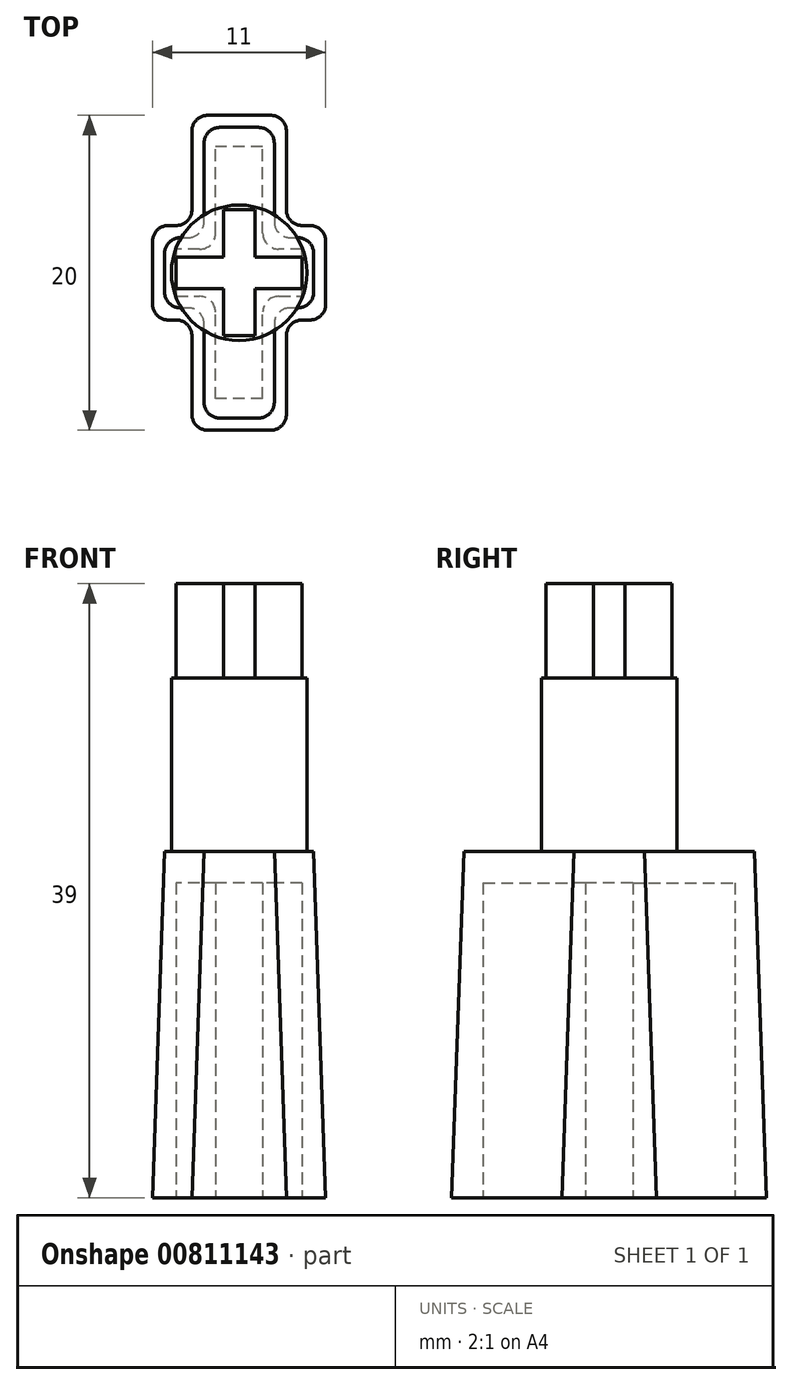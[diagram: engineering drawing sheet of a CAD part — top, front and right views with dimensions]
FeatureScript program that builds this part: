
annotation { "Feature Type Name" : "Feature", "Feature Type Description" : "" }
export const myFeature = defineFeature(function(context is Context, id is Id, definition is map)
    precondition{}
    {
        {
            var Q0;
            Q0=qCreatedBy(makeId("Top.planeOp"),FACE);
            var sketch = newSketch(context, id + "F0", { "sketchPlane" : qUnion([Q0])});
            skLineSegment(sketch, "E0.bottom", {"start": v(1.5, -8) * mm, "end": v(-1.5, -8) * mm});
            skLineSegment(sketch, "E0.top", {"start": v(1.5, 8) * mm, "end": v(-1.5, 8) * mm});
            skLineSegment(sketch, "E0.left", {"start": v(1.5, -8) * mm, "end": v(1.5, 8) * mm});
            skLineSegment(sketch, "E0.right", {"start": v(-1.5, -8) * mm, "end": v(-1.5, 8) * mm});
            skPoint(sketch, "E0.middle", {"position": v(0, 0) * mm});
            skLineSegment(sketch, "E1", {"start": v(-1.5, 1.5) * mm, "end": v(-4, 1.5) * mm});
            skLineSegment(sketch, "E2", {"start": v(-4, 1.5) * mm, "end": v(-4, -1.5) * mm});
            skLineSegment(sketch, "E3", {"start": v(-4, -1.5) * mm, "end": v(-1.5, -1.5) * mm});
            skLineSegment(sketch, "E4", {"start": v(1.5, 1.5) * mm, "end": v(1.5, -1.5) * mm});
            skLineSegment(sketch, "E5", {"start": v(1.5, -1.5) * mm, "end": v(4, -1.5) * mm});
            skLineSegment(sketch, "E6", {"start": v(4, -1.5) * mm, "end": v(4, 1.5) * mm});
            skLineSegment(sketch, "E7", {"start": v(4, 1.5) * mm, "end": v(1.5, 1.5) * mm});
            skPoint(sketch, "E8", {"position": v(-4, 0) * mm});
            skPoint(sketch, "E9", {"position": v(4, 0) * mm});
            skSolve(sketch);
        }
        {
            var Q0;
            Q0=qCreatedBy(makeId("Top.planeOp"),FACE);
            var sketch = newSketch(context, id + "F1", { "sketchPlane" : qUnion([Q0])});
            skLineSegment(sketch, "E10.bottom", {"start": v(3, 10) * mm, "end": v(-3, 10) * mm});
            skLineSegment(sketch, "E10.top", {"start": v(3, -10) * mm, "end": v(-3, -10) * mm});
            skLineSegment(sketch, "E10.left", {"start": v(3, 10) * mm, "end": v(3, -10) * mm});
            skLineSegment(sketch, "E10.right", {"start": v(-3, 10) * mm, "end": v(-3, -10) * mm});
            skPoint(sketch, "E10.middle", {"position": v(0, 0) * mm});
            skPoint(sketch, "E11", {"position": v(-3, -3) * mm});
            skPoint(sketch, "E12", {"position": v(-3, 3) * mm});
            skPoint(sketch, "E13", {"position": v(3, 3) * mm});
            skPoint(sketch, "E14", {"position": v(3, -3) * mm});
            skLineSegment(sketch, "E15", {"start": v(-3, 3) * mm, "end": v(-5.5, 3) * mm});
            skLineSegment(sketch, "E16", {"start": v(-5.5, 3) * mm, "end": v(-5.5, -3) * mm});
            skLineSegment(sketch, "E17", {"start": v(-5.5, -3) * mm, "end": v(-3, -3) * mm});
            skLineSegment(sketch, "E18", {"start": v(3, 3) * mm, "end": v(5.5, 3) * mm});
            skLineSegment(sketch, "E19", {"start": v(5.5, 3) * mm, "end": v(5.5, -3) * mm});
            skLineSegment(sketch, "E20", {"start": v(5.5, -3) * mm, "end": v(3, -3) * mm});
            skPoint(sketch, "E21", {"position": v(-5.5, 0) * mm});
            skPoint(sketch, "E22", {"position": v(5.5, 0) * mm});
            skSolve(sketch);
        }
        {
            var Q0;
            Q0=makeQuery(id+"F1.imprint","IMPRINT",FACE,{"disambiguationData":[TD([[makeQuery(id+"F1.imprint","IMPRINT",EDGE,{"derivedFrom":sQuery(id+"F1.wireOp",EDGE,"E10.bottom")}),1.0]])]});
            var Q1;
            {var subQ0=sQuery(id+"F1.wireOp",EDGE,"E15");Q1=makeQuery(id+"F1.imprint","IMPRINT",FACE,{"disambiguationData":[TD([[makeQuery(id+"F1.imprint","IMPRINT",EDGE,{"derivedFrom":subQ0}),1.0]])]});}
            var Q2;
            {var subQ0=sQuery(id+"F1.wireOp",EDGE,"E18");Q2=makeQuery(id+"F1.imprint","IMPRINT",FACE,{"disambiguationData":[TD([[makeQuery(id+"F1.imprint","IMPRINT",EDGE,{"derivedFrom":subQ0}),-1.0]])]});}
            extrude(context, id + "F2", {"entities" : qUnion([Q0, Q1, Q2]), "depth" : 22 * mm, "offsetDistance" : 25 * mm, "hasDraft" : true, "draftAngle" : 2 * degree, "draftPullDirection" : true});
        }
        {
            var Q0;
            Q0 = qSketchRegion(id + "F0", true);
            extrude(context, id + "F3", {"entities" : qUnion([Q0]), "operationType" : NewBodyOperationType.REMOVE, "depth" : 20 * mm, "offsetDistance" : 25 * mm});
        }
        {
            var Q0;
            Q0=makeQuery(id+"F2.opExtrude","CAP_FACE",FACE,{"disambiguationData":[OSD([sQuery(id+"F1.wireOp",EDGE,"E10.bottom"),sQuery(id+"F1.wireOp",EDGE,"E10.top"),sQuery(id+"F1.wireOp",EDGE,"E10.left"),sQuery(id+"F1.wireOp",EDGE,"E10.right")])],"isStart":false});
            cPlane(context, id + "F4", {"entities" : qUnion([Q0]), "cplaneType" : CPlaneType.OFFSET, "offset" : 11 * mm, "width" : 150 * mm, "height" : 150 * mm});
        }
        {
            var Q0;
            Q0=qCreatedBy(id+"F4.planeOp",FACE);
            var sketch = newSketch(context, id + "F5", { "sketchPlane" : qUnion([Q0])});
            skLineSegment(sketch, "E23.bottom", {"start": v(4.5, -3) * mm, "end": v(-4.5, -3) * mm});
            skLineSegment(sketch, "E23.top", {"start": v(4.5, 3) * mm, "end": v(-4.5, 3) * mm});
            skLineSegment(sketch, "E23.left", {"start": v(4.5, -3) * mm, "end": v(4.5, 3) * mm});
            skLineSegment(sketch, "E23.right", {"start": v(-4.5, -3) * mm, "end": v(-4.5, 3) * mm});
            skPoint(sketch, "E23.middle", {"position": v(0, 0) * mm});
            skLineSegment(sketch, "E24.bottom", {"start": v(3, 5.5) * mm, "end": v(-3, 5.5) * mm});
            skLineSegment(sketch, "E24.top", {"start": v(3, -5.5) * mm, "end": v(-3, -5.5) * mm});
            skLineSegment(sketch, "E24.left", {"start": v(3, 5.5) * mm, "end": v(3, -5.5) * mm});
            skLineSegment(sketch, "E24.right", {"start": v(-3, 5.5) * mm, "end": v(-3, -5.5) * mm});
            skLineSegment(sketch, "E25.bottom", {"start": v(4, -1) * mm, "end": v(-4, -1) * mm});
            skLineSegment(sketch, "E25.top", {"start": v(4, 1) * mm, "end": v(-4, 1) * mm});
            skLineSegment(sketch, "E25.left", {"start": v(4, -1) * mm, "end": v(4, 1) * mm});
            skLineSegment(sketch, "E25.right", {"start": v(-4, -1) * mm, "end": v(-4, 1) * mm});
            skLineSegment(sketch, "E26.bottom", {"start": v(-1, 4) * mm, "end": v(1, 4) * mm});
            skLineSegment(sketch, "E26.top", {"start": v(-1, -4) * mm, "end": v(1, -4) * mm});
            skLineSegment(sketch, "E26.left", {"start": v(-1, 4) * mm, "end": v(-1, -4) * mm});
            skLineSegment(sketch, "E26.right", {"start": v(1, 4) * mm, "end": v(1, -4) * mm});
            skSolve(sketch);
        }
        {
            var Q0;
            Q0=makeQuery(id+"F2.opExtrude","SWEPT_EDGE",EDGE,{"disambiguationData":[OSD([sQuery(id+"F1.wireOp",EDGE,"E16"),sQuery(id+"F1.wireOp",EDGE,"E17")])]});
            var Q1;
            Q1=makeQuery(id+"F2.opExtrude","SWEPT_EDGE",EDGE,{"disambiguationData":[OSD([sQuery(id+"F1.wireOp",EDGE,"E15"),sQuery(id+"F1.wireOp",EDGE,"E16")])]});
            var Q2;
            Q2=makeQuery(id+"F2.opExtrude","SWEPT_EDGE",EDGE,{"disambiguationData":[OSD([sQuery(id+"F1.wireOp",EDGE,"E10.top"),sQuery(id+"F1.wireOp",EDGE,"E10.right")])]});
            var Q3;
            Q3=makeQuery(id+"F2.opExtrude","SWEPT_EDGE",EDGE,{"disambiguationData":[OSD([sQuery(id+"F1.wireOp",EDGE,"E10.top"),sQuery(id+"F1.wireOp",EDGE,"E10.left")])]});
            var Q4;
            Q4=makeQuery(id+"F2.opExtrude","SWEPT_EDGE",EDGE,{"disambiguationData":[OSD([sQuery(id+"F1.wireOp",EDGE,"E10.bottom"),sQuery(id+"F1.wireOp",EDGE,"E10.right")])]});
            var Q5;
            Q5=makeQuery(id+"F2.opExtrude","SWEPT_EDGE",EDGE,{"disambiguationData":[OSD([sQuery(id+"F1.wireOp",EDGE,"E10.bottom"),sQuery(id+"F1.wireOp",EDGE,"E10.left")])]});
            var Q6;
            Q6=makeQuery(id+"F2.opExtrude","SWEPT_EDGE",EDGE,{"disambiguationData":[OSD([sQuery(id+"F1.wireOp",EDGE,"E18"),sQuery(id+"F1.wireOp",EDGE,"E19")])]});
            var Q7;
            Q7=makeQuery(id+"F2.opExtrude","SWEPT_EDGE",EDGE,{"disambiguationData":[OSD([sQuery(id+"F1.wireOp",EDGE,"E19"),sQuery(id+"F1.wireOp",EDGE,"E20")])]});
            var Q8;
            Q8=makeQuery(id+"F2.opExtrude","SWEPT_EDGE",EDGE,{"disambiguationData":[OSD([sQuery(id+"F1.wireOp",EDGE,"E10.left"),sQuery(id+"F1.wireOp",EDGE,"E18")])]});
            var Q9;
            Q9=makeQuery(id+"F2.opExtrude","SWEPT_EDGE",EDGE,{"disambiguationData":[OSD([sQuery(id+"F1.wireOp",EDGE,"E10.left"),sQuery(id+"F1.wireOp",EDGE,"E20")])]});
            var Q10;
            Q10=makeQuery(id+"F2.opExtrude","SWEPT_EDGE",EDGE,{"disambiguationData":[OSD([sQuery(id+"F1.wireOp",EDGE,"E10.right"),sQuery(id+"F1.wireOp",EDGE,"E15")])]});
            var Q11;
            Q11=makeQuery(id+"F2.opExtrude","SWEPT_EDGE",EDGE,{"disambiguationData":[OSD([sQuery(id+"F1.wireOp",EDGE,"E10.right"),sQuery(id+"F1.wireOp",EDGE,"E17")])]});
            var Q12;
            Q12=makeQuery(id+"F3.boolean.opBoolean","COPY",EDGE,{"derivedFrom":makeQuery(id+"F3.opExtrude","SWEPT_EDGE",EDGE,{"disambiguationData":[OSD([sQuery(id+"F0.wireOp",EDGE,"E0.right"),sQuery(id+"F0.wireOp",EDGE,"E3")])]})});
            var Q13;
            Q13=makeQuery(id+"F3.boolean.opBoolean","COPY",EDGE,{"derivedFrom":makeQuery(id+"F3.opExtrude","SWEPT_EDGE",EDGE,{"disambiguationData":[OSD([sQuery(id+"F0.wireOp",EDGE,"E0.right"),sQuery(id+"F0.wireOp",EDGE,"E1")])]})});
            var Q14;
            Q14=makeQuery(id+"F3.boolean.opBoolean","COPY",EDGE,{"derivedFrom":makeQuery(id+"F3.opExtrude","SWEPT_EDGE",EDGE,{"disambiguationData":[OSD([sQuery(id+"F0.wireOp",EDGE,"E0.left"),sQuery(id+"F0.wireOp",EDGE,"E4"),sQuery(id+"F0.wireOp",EDGE,"E7")])]})});
            var Q15;
            Q15=makeQuery(id+"F3.boolean.opBoolean","COPY",EDGE,{"derivedFrom":makeQuery(id+"F3.opExtrude","SWEPT_EDGE",EDGE,{"disambiguationData":[OSD([sQuery(id+"F0.wireOp",EDGE,"E0.left"),sQuery(id+"F0.wireOp",EDGE,"E4"),sQuery(id+"F0.wireOp",EDGE,"E5")])]})});
            fillet(context, id + "F6", {"entities" : qUnion([Q0, Q1, Q2, Q3, Q4, Q5, Q6, Q7, Q8, Q9, Q10, Q11, Q12, Q13, Q14, Q15]), "radius" : 1 * mm, "tangentPropagation" : true, "allowEdgeOverflow" : false});
        }
        {
            var Q0;
            Q0=qCreatedBy(id+"F4.planeOp",FACE);
            var sketch = newSketch(context, id + "F7", { "sketchPlane" : qUnion([Q0])});
            skCircle(sketch, "E27", {"center": v(0, 0) * mm, "radius": 4.3 * mm});
            skSolve(sketch);
        }
        {
            var Q0;
            Q0 = qSketchRegion(id + "F7", true);
            extrude(context, id + "F8", {"entities" : qUnion([Q0]), "operationType" : NewBodyOperationType.ADD, "oppositeDirection" : true, "depth" : 11 * mm, "offsetDistance" : 25 * mm});
        }
        {
            var Q0;
            {var subQ0=sQuery(id+"F5.wireOp",EDGE,"E26.right");var subQ1=sQuery(id+"F5.wireOp",EDGE,"E25.bottom");var subQ2=makeQuery(id+"F5.imprint","INTERSECT",VERTEX,{"derivedFrom":[subQ1,subQ0]});Q0=makeQuery(id+"F5.imprint","IMPRINT",FACE,{"disambiguationData":[TD([[makeQuery(id+"F5.imprint","IMPRINT",EDGE,{"disambiguationData":[TD([[subQ2,-1.0]])],"derivedFrom":subQ1}),-1.0]])]});}
            var Q1;
            {var subQ0=sQuery(id+"F5.wireOp",EDGE,"E26.right");var subQ1=sQuery(id+"F5.wireOp",EDGE,"E23.bottom");var subQ2=makeQuery(id+"F5.imprint","INTERSECT",VERTEX,{"derivedFrom":[subQ1,subQ0]});Q1=makeQuery(id+"F5.imprint","IMPRINT",FACE,{"disambiguationData":[TD([[makeQuery(id+"F5.imprint","IMPRINT",EDGE,{"disambiguationData":[TD([[subQ2,-1.0]])],"derivedFrom":subQ1}),-1.0]])]});}
            var Q2;
            {var subQ0=sQuery(id+"F5.wireOp",EDGE,"E25.top");var subQ1=sQuery(id+"F5.wireOp",EDGE,"E24.right");var subQ2=makeQuery(id+"F5.imprint","INTERSECT",VERTEX,{"derivedFrom":[subQ1,subQ0]});Q2=makeQuery(id+"F5.imprint","IMPRINT",FACE,{"disambiguationData":[TD([[makeQuery(id+"F5.imprint","IMPRINT",EDGE,{"disambiguationData":[TD([[subQ2,-1.0]])],"derivedFrom":subQ1}),1.0]])]});}
            var Q3;
            {var subQ0=sQuery(id+"F5.wireOp",EDGE,"E25.top");var subQ1=sQuery(id+"F5.wireOp",EDGE,"E24.left");var subQ2=makeQuery(id+"F5.imprint","INTERSECT",VERTEX,{"derivedFrom":[subQ1,subQ0]});Q3=makeQuery(id+"F5.imprint","IMPRINT",FACE,{"disambiguationData":[TD([[makeQuery(id+"F5.imprint","IMPRINT",EDGE,{"disambiguationData":[TD([[subQ2,-1.0]])],"derivedFrom":subQ1}),-1.0]])]});}
            var Q4;
            {var subQ0=sQuery(id+"F5.wireOp",EDGE,"E26.right");var subQ1=sQuery(id+"F5.wireOp",EDGE,"E23.top");var subQ2=makeQuery(id+"F5.imprint","INTERSECT",VERTEX,{"derivedFrom":[subQ1,subQ0]});Q4=makeQuery(id+"F5.imprint","IMPRINT",FACE,{"disambiguationData":[TD([[makeQuery(id+"F5.imprint","IMPRINT",EDGE,{"disambiguationData":[TD([[subQ2,-1.0]])],"derivedFrom":subQ1}),1.0]])]});}
            var Q5;
            {var subQ5=sQuery(id+"F5.wireOp",EDGE,"E26.top");Q5=makeQuery(id+"F5.imprint","IMPRINT",FACE,{"disambiguationData":[TD([[makeQuery(id+"F5.imprint","IMPRINT",EDGE,{"derivedFrom":subQ5}),1.0]])]});}
            var Q6;
            {var subQ5=sQuery(id+"F5.wireOp",EDGE,"E25.right");Q6=makeQuery(id+"F5.imprint","IMPRINT",FACE,{"disambiguationData":[TD([[makeQuery(id+"F5.imprint","IMPRINT",EDGE,{"derivedFrom":subQ5}),-1.0]])]});}
            var Q7;
            {var subQ5=sQuery(id+"F5.wireOp",EDGE,"E26.bottom");Q7=makeQuery(id+"F5.imprint","IMPRINT",FACE,{"disambiguationData":[TD([[makeQuery(id+"F5.imprint","IMPRINT",EDGE,{"derivedFrom":subQ5}),-1.0]])]});}
            var Q8;
            {var subQ5=sQuery(id+"F5.wireOp",EDGE,"E25.left");Q8=makeQuery(id+"F5.imprint","IMPRINT",FACE,{"disambiguationData":[TD([[makeQuery(id+"F5.imprint","IMPRINT",EDGE,{"derivedFrom":subQ5}),1.0]])]});}
            extrude(context, id + "F9", {"entities" : qUnion([Q0, Q1, Q2, Q3, Q4, Q5, Q6, Q7, Q8]), "operationType" : NewBodyOperationType.ADD, "depth" : 6 * mm, "offsetDistance" : 25 * mm});
        }
    });
